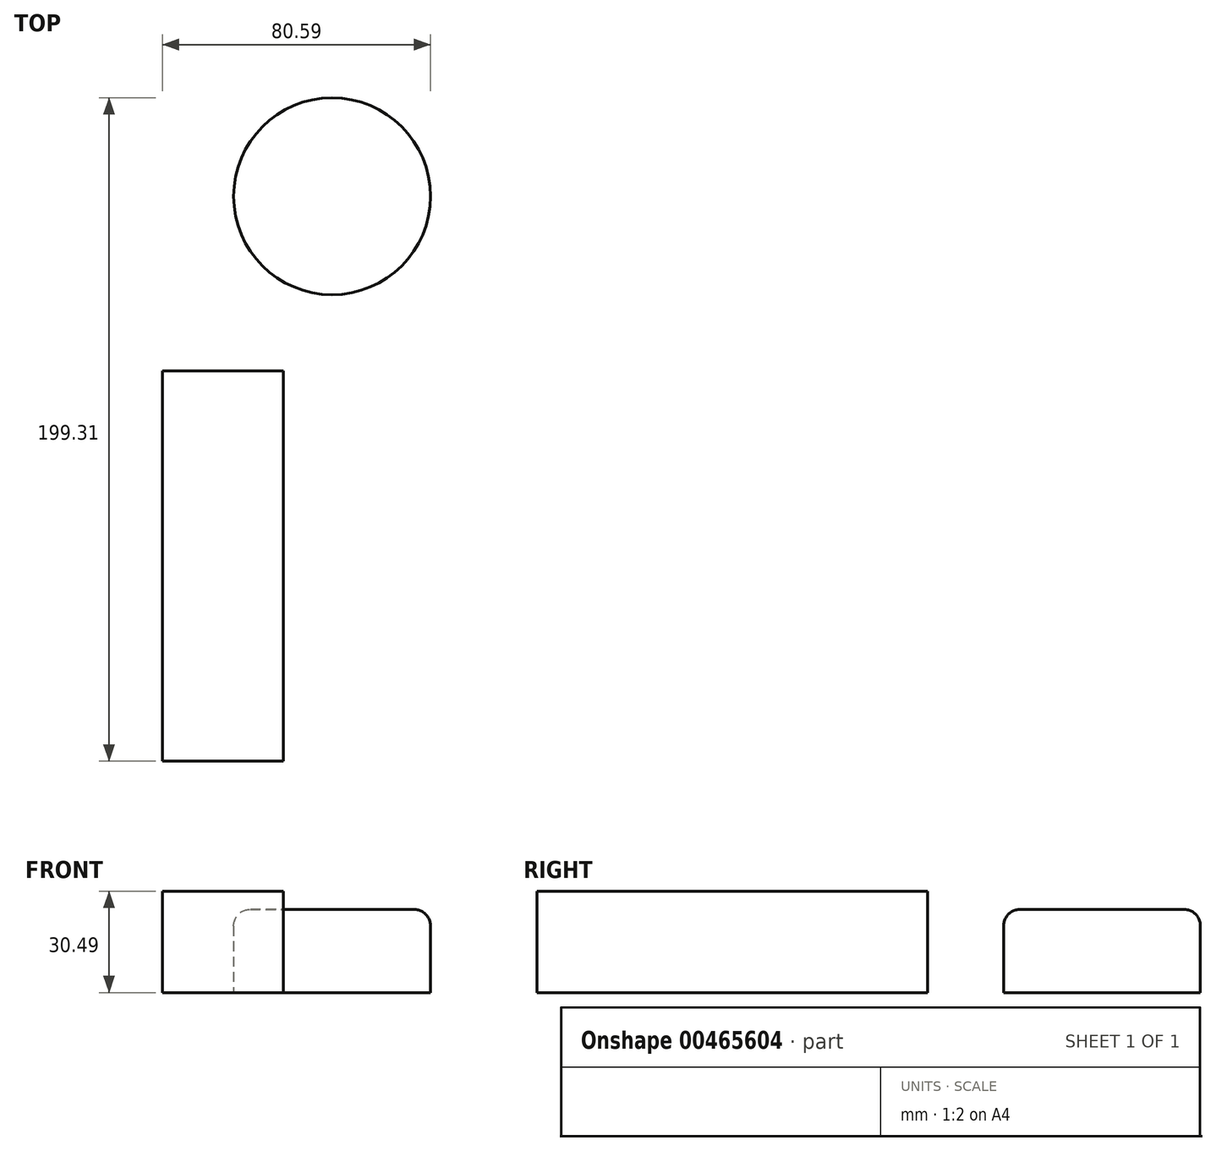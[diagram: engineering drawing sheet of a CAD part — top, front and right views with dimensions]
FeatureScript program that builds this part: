
annotation { "Feature Type Name" : "Feature", "Feature Type Description" : "" }
export const myFeature = defineFeature(function(context is Context, id is Id, definition is map)
    precondition{}
    {
        {
            var Q0;
            Q0=qCreatedBy(makeId("Front.planeOp"),FACE);
            var sketch = newSketch(context, id + "F0", { "sketchPlane" : qUnion([Q0])});
            skLineSegment(sketch, "E0.bottom", {"start": v(-55.01, 55.85) * mm, "end": v(55.01, 55.85) * mm});
            skLineSegment(sketch, "E0.top", {"start": v(-55.01, -55.85) * mm, "end": v(55.01, -55.85) * mm});
            skLineSegment(sketch, "E0.left", {"start": v(-55.01, 55.85) * mm, "end": v(-55.01, -55.85) * mm});
            skLineSegment(sketch, "E0.right", {"start": v(55.01, 55.85) * mm, "end": v(55.01, -55.85) * mm});
            skPoint(sketch, "E0.middle", {"position": v(0, 0) * mm});
            skSolve(sketch);
        }
        {
            var Q0;
            Q0=makeQuery(id+"F0.imprint","IMPRINT",FACE,{"disambiguationData":[TD([[makeQuery(id+"F0.imprint","IMPRINT",EDGE,{"derivedFrom":sQuery(id+"F0.wireOp",EDGE,"E0.bottom")}),-1.0]])]});
            extrude(context, id + "F1", {"entities" : qUnion([Q0]), "depth" : 50 * mm});
        }
        {
            var Q0;
            Q0=makeQuery(id+"F1.opExtrude","SWEPT_EDGE",EDGE,{"disambiguationData":[OSD([sQuery(id+"F0.wireOp",EDGE,"E0.bottom"),sQuery(id+"F0.wireOp",EDGE,"E0.left")])]});
            var Q1;
            Q1=makeQuery(id+"F1.opExtrude","SWEPT_EDGE",EDGE,{"disambiguationData":[OSD([sQuery(id+"F0.wireOp",EDGE,"E0.bottom"),sQuery(id+"F0.wireOp",EDGE,"E0.right")])]});
            var Q2;
            Q2=makeQuery(id+"F1.opExtrude","CAP_FACE",FACE,{"disambiguationData":[OSD([sQuery(id+"F0.wireOp",EDGE,"E0.bottom"),sQuery(id+"F0.wireOp",EDGE,"E0.top"),sQuery(id+"F0.wireOp",EDGE,"E0.left"),sQuery(id+"F0.wireOp",EDGE,"E0.right")])],"isStart":false});
            fillet(context, id + "F2", {"entities" : qUnion([Q0, Q1, Q2]), "radius" : 5 * mm, "tangentPropagation" : true, "allowEdgeOverflow" : false});
        }
        {
            var Q0;
            Q0=makeQuery(id+"F1.opExtrude","SWEPT_BODY",BODY,{"disambiguationData":[OSD([sQuery(id+"F0.wireOp",EDGE,"E0.bottom"),sQuery(id+"F0.wireOp",EDGE,"E0.top"),sQuery(id+"F0.wireOp",EDGE,"E0.left"),sQuery(id+"F0.wireOp",EDGE,"E0.right")])]});
            deleteBodies(context, id + "F3", {"entities" : qUnion([Q0])});
        }
        {
            var Q0;
            Q0=qCreatedBy(makeId("Front.planeOp"),FACE);
            var sketch = newSketch(context, id + "F4", { "sketchPlane" : qUnion([Q0])});
            skLineSegment(sketch, "E1.bottom", {"start": v(36.44, 30.5) * mm, "end": v(0, 30.5) * mm});
            skLineSegment(sketch, "E1.top", {"start": v(36.44, 0) * mm, "end": v(0, 0) * mm});
            skLineSegment(sketch, "E1.left", {"start": v(36.44, 30.5) * mm, "end": v(36.44, 0) * mm});
            skLineSegment(sketch, "E1.right", {"start": v(0, 30.5) * mm, "end": v(0, 0) * mm});
            skLineSegment(sketch, "E2.bottom", {"start": v(58.38, 4.35) * mm, "end": v(53.2, 4.35) * mm});
            skLineSegment(sketch, "E2.top", {"start": v(58.38, 0) * mm, "end": v(53.2, 0) * mm});
            skLineSegment(sketch, "E2.left", {"start": v(58.38, 4.35) * mm, "end": v(58.38, 0) * mm});
            skLineSegment(sketch, "E2.right", {"start": v(53.2, 4.35) * mm, "end": v(53.2, 0) * mm});
            skSolve(sketch);
        }
        {
            var Q0;
            Q0=makeQuery(id+"F4.imprint","IMPRINT",FACE,{"disambiguationData":[TD([[makeQuery(id+"F4.imprint","IMPRINT",EDGE,{"derivedFrom":sQuery(id+"F4.wireOp",EDGE,"E1.bottom")}),1.0]])]});
            extrude(context, id + "F5", {"entities" : qUnion([Q0]), "depth" : 117.31 * mm});
        }
        {
            var Q0;
            Q0=qCreatedBy(makeId("Top.planeOp"),FACE);
            var sketch = newSketch(context, id + "F6", { "sketchPlane" : qUnion([Q0])});
            skCircle(sketch, "E3", {"center": v(51.02, 52.43) * mm, "radius": 29.57 * mm});
            skSolve(sketch);
        }
        {
            var Q0;
            Q0=makeQuery(id+"F6.imprint","IMPRINT",FACE,{"disambiguationData":[TD([[makeQuery(id+"F6.imprint","IMPRINT",EDGE,{"derivedFrom":sQuery(id+"F6.wireOp",EDGE,"E3")}),1.0]])]});
            extrude(context, id + "F7", {"entities" : qUnion([Q0]), "depth" : 25 * mm});
        }
        {
            var Q0;
            Q0=makeQuery(id+"F7.opExtrude","CAP_EDGE",EDGE,{"disambiguationData":[OSD([sQuery(id+"F6.wireOp",EDGE,"E3")])],"isStart":false});
            fillet(context, id + "F8", {"entities" : qUnion([Q0]), "radius" : 5 * mm, "tangentPropagation" : true, "allowEdgeOverflow" : false});
        }
    });
